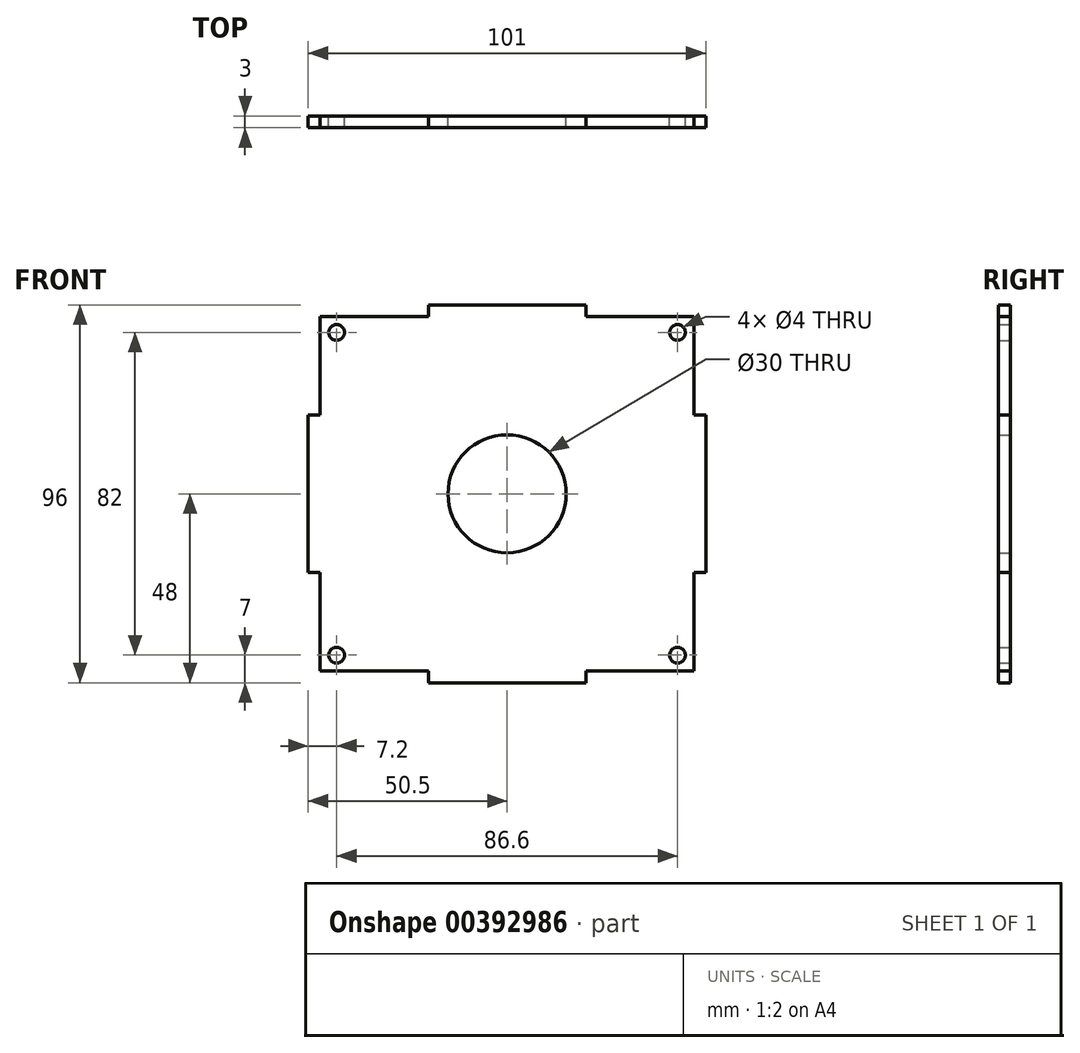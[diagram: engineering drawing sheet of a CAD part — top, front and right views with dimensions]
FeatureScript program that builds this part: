
annotation { "Feature Type Name" : "Feature", "Feature Type Description" : "" }
export const myFeature = defineFeature(function(context is Context, id is Id, definition is map)
    precondition{}
    {
        {
            var Q0;
            Q0=qCreatedBy(makeId("Front.planeOp"),FACE);
            var sketch = newSketch(context, id + "F0", { "sketchPlane" : qUnion([Q0])});
            skLineSegment(sketch, "E0", {"start": v(-50.5, 0) * mm, "end": v(-50.5, 20) * mm});
            skLineSegment(sketch, "E1", {"start": v(-50.5, 20) * mm, "end": v(-47.5, 20) * mm});
            skLineSegment(sketch, "E2", {"start": v(-47.5, 20) * mm, "end": v(-47.5, 45) * mm});
            skLineSegment(sketch, "E3", {"start": v(-47.5, 45) * mm, "end": v(-20, 45) * mm});
            skLineSegment(sketch, "E4", {"start": v(-20, 45) * mm, "end": v(-20, 48) * mm});
            skLineSegment(sketch, "E5", {"start": v(-20, 48) * mm, "end": v(0, 48) * mm});
            skLineSegment(sketch, "E6", {"start": v(-50.5, 0) * mm, "end": v(0, 0) * mm, "construction": true});
            skLineSegment(sketch, "E7", {"start": v(0, 0) * mm, "end": v(0, 48) * mm, "construction": true});
            skLineSegment(sketch, "E8.MirrorCS", {"start": v(50.5, 20) * mm, "end": v(47.5, 20) * mm});
            skLineSegment(sketch, "E9.MirrorCS", {"start": v(47.5, 20) * mm, "end": v(47.5, 45) * mm});
            skLineSegment(sketch, "E10.MirrorCS", {"start": v(47.5, 45) * mm, "end": v(20, 45) * mm});
            skLineSegment(sketch, "E11.MirrorCS", {"start": v(20, 45) * mm, "end": v(20, 48) * mm});
            skLineSegment(sketch, "E12.MirrorCS", {"start": v(50.5, 0) * mm, "end": v(50.5, 20) * mm});
            skLineSegment(sketch, "E13.MirrorCS", {"start": v(20, 48) * mm, "end": v(0, 48) * mm});
            skLineSegment(sketch, "E14.MirrorCS", {"start": v(50.5, -20) * mm, "end": v(47.5, -20) * mm});
            skLineSegment(sketch, "E15.MirrorCS", {"start": v(-20, -48) * mm, "end": v(0, -48) * mm});
            skLineSegment(sketch, "E16.MirrorCS", {"start": v(-50.5, 0) * mm, "end": v(-50.5, -20) * mm});
            skLineSegment(sketch, "E17.MirrorCS", {"start": v(47.5, -45) * mm, "end": v(20, -45) * mm});
            skLineSegment(sketch, "E18.MirrorCS", {"start": v(-50.5, -20) * mm, "end": v(-47.5, -20) * mm});
            skLineSegment(sketch, "E19.MirrorCS", {"start": v(-47.5, -20) * mm, "end": v(-47.5, -45) * mm});
            skLineSegment(sketch, "E20.MirrorCS", {"start": v(47.5, -20) * mm, "end": v(47.5, -45) * mm});
            skLineSegment(sketch, "E21.MirrorCS", {"start": v(20, -45) * mm, "end": v(20, -48) * mm});
            skLineSegment(sketch, "E22.MirrorCS", {"start": v(20, -48) * mm, "end": v(0, -48) * mm});
            skLineSegment(sketch, "E23.MirrorCS", {"start": v(-20, -45) * mm, "end": v(-20, -48) * mm});
            skLineSegment(sketch, "E24.MirrorCS", {"start": v(50.5, 0) * mm, "end": v(50.5, -20) * mm});
            skLineSegment(sketch, "E25.MirrorCS", {"start": v(-47.5, -45) * mm, "end": v(-20, -45) * mm});
            skCircle(sketch, "E26", {"center": v(-43.3, 41) * mm, "radius": 2 * mm});
            skLineSegment(sketch, "E27.MirrorCS", {"start": v(50.5, 0) * mm, "end": v(0, 0) * mm, "construction": true});
            skCircle(sketch, "E28.MirrorC", {"center": v(43.3, 41) * mm, "radius": 2 * mm});
            skCircle(sketch, "E29.MirrorC", {"center": v(-43.3, -41) * mm, "radius": 2 * mm});
            skCircle(sketch, "E30.MirrorC", {"center": v(43.3, -41) * mm, "radius": 2 * mm});
            skCircle(sketch, "E31", {"center": v(0, 0) * mm, "radius": 15 * mm});
            skSolve(sketch);
        }
        {
            var Q0;
            Q0=qSketchRegion(id+"F0",true);
            extrude(context, id + "F1", {"entities" : qUnion([Q0]), "depth" : 3 * mm});
        }
    });
